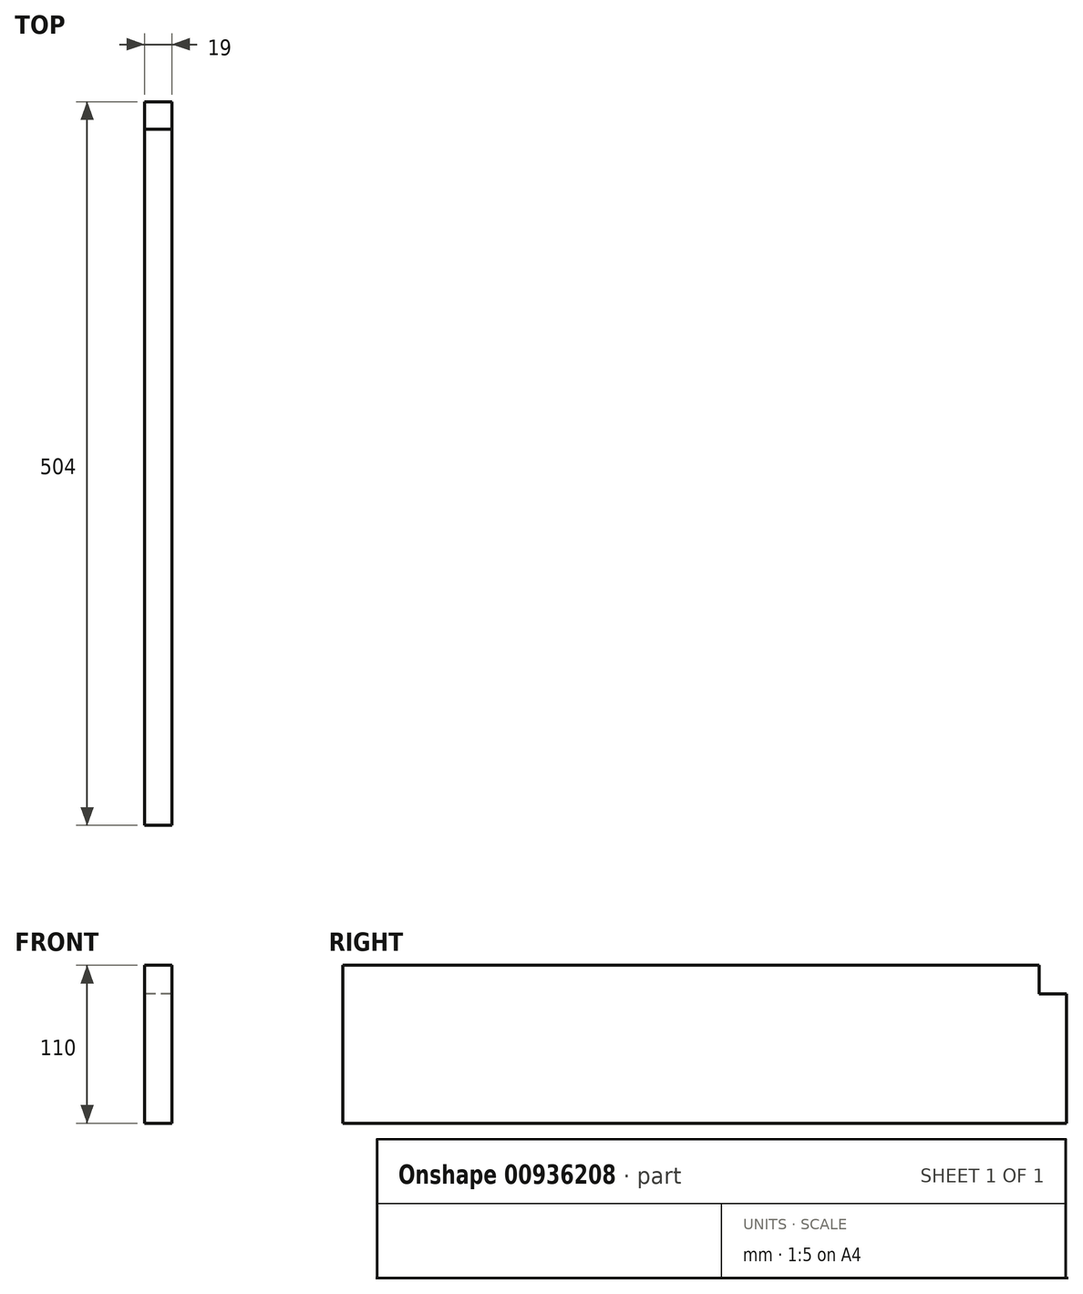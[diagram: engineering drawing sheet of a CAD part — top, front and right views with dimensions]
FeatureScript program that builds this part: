
annotation { "Feature Type Name" : "Feature", "Feature Type Description" : "" }
export const myFeature = defineFeature(function(context is Context, id is Id, definition is map)
    precondition{}
    {
        {
            var Q0;
            Q0=qCreatedBy(makeId("Front.planeOp"),FACE);
            var sketch = newSketch(context, id + "F0", { "sketchPlane" : qUnion([Q0])});
            skLineSegment(sketch, "E0.bottom", {"start": v(0, 0) * mm, "end": v(19, 0) * mm});
            skLineSegment(sketch, "E0.top", {"start": v(0, 90) * mm, "end": v(19, 90) * mm});
            skLineSegment(sketch, "E0.left", {"start": v(0, 0) * mm, "end": v(0, 90) * mm});
            skLineSegment(sketch, "E0.right", {"start": v(19, 0) * mm, "end": v(19, 90) * mm});
            skSolve(sketch);
        }
        {
            var Q0;
            Q0=qSketchRegion(id+"F0",true);
            extrude(context, id + "F1", {"entities" : qUnion([Q0]), "depth" : 504 * mm, "offsetDistance" : 25 * mm});
        }
        {
            var Q0;
            Q0=qCreatedBy(makeId("Right.planeOp"),FACE);
            var sketch = newSketch(context, id + "F2", { "sketchPlane" : qUnion([Q0])});
            skLineSegment(sketch, "E1.0", {"start": v(-504, 90) * mm, "end": v(0, 90) * mm, "construction": true});
            skLineSegment(sketch, "E2.bottom", {"start": v(-504, 90) * mm, "end": v(-19, 90) * mm});
            skLineSegment(sketch, "E2.top", {"start": v(-504, 110) * mm, "end": v(-19, 110) * mm});
            skLineSegment(sketch, "E2.left", {"start": v(-504, 90) * mm, "end": v(-504, 110) * mm});
            skLineSegment(sketch, "E2.right", {"start": v(-19, 90) * mm, "end": v(-19, 110) * mm});
            skSolve(sketch);
        }
        {
            var Q0;
            Q0 = qSketchRegion(id + "F2", true);
            var Q1;
            Q1=makeQuery(id+"F1.opExtrude","SWEPT_FACE",FACE,{"disambiguationData":[OSD([sQuery(id+"F0.wireOp",EDGE,"E0.right")])]});
            extrude(context, id + "F3", {"entities" : qUnion([Q0]), "operationType" : NewBodyOperationType.ADD, "endBound" : BoundingType.UP_TO_SURFACE, "depth" : 19 * mm, "endBoundEntityFace" : qUnion([Q1]), "offsetDistance" : 25 * mm});
        }
    });
